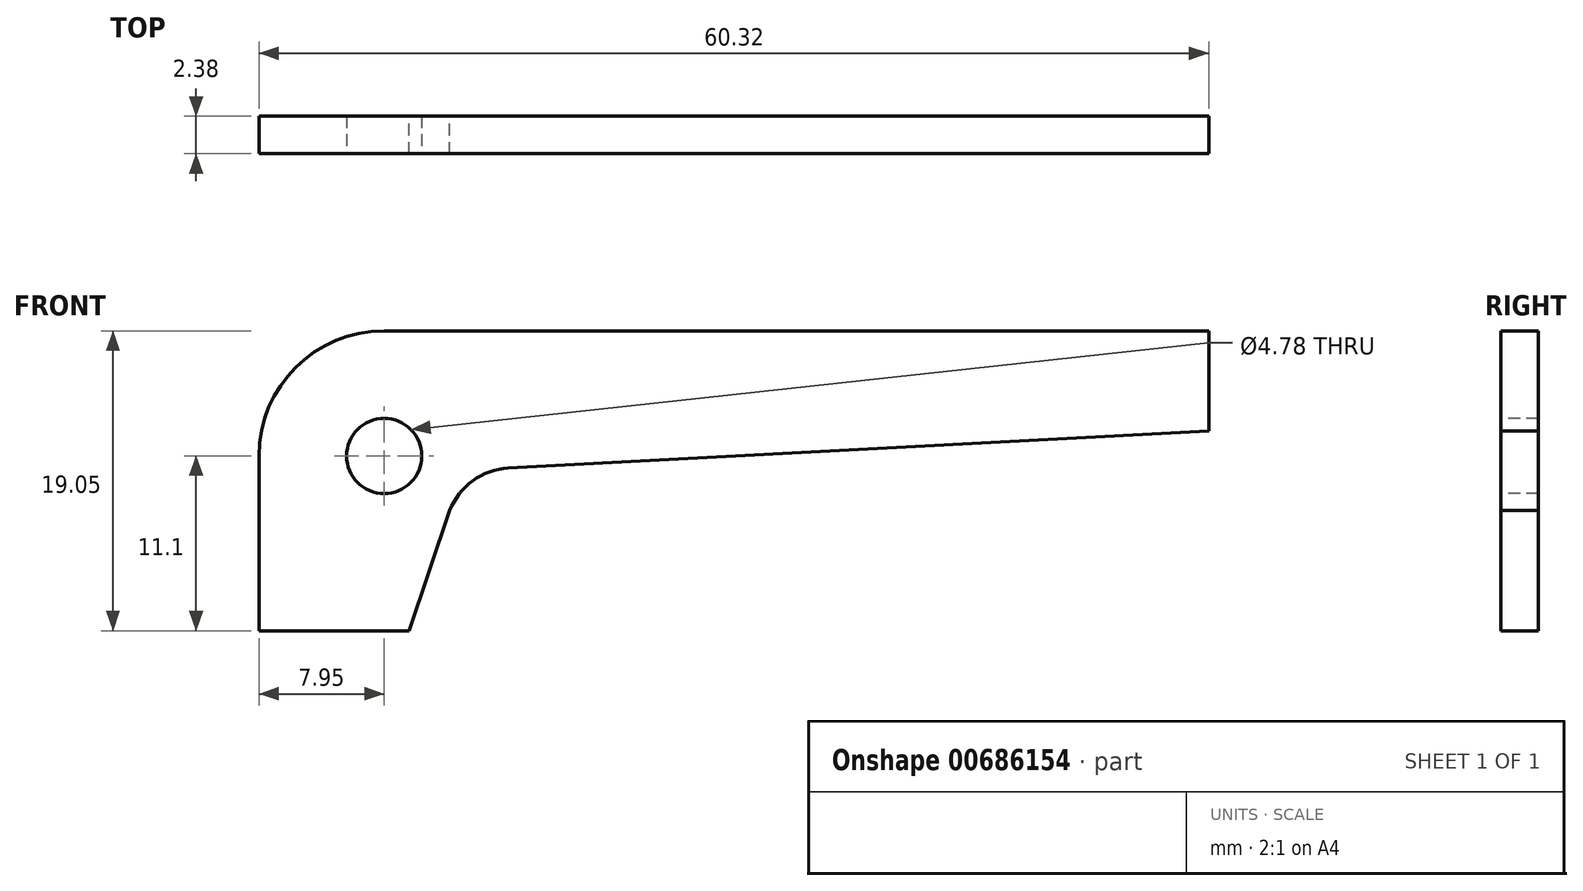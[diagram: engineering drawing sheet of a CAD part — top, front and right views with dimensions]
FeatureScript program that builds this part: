
annotation { "Feature Type Name" : "Feature", "Feature Type Description" : "" }
export const myFeature = defineFeature(function(context is Context, id is Id, definition is map)
    precondition{}
    {
        {
            var Q0;
            Q0=qCreatedBy(makeId("Front.planeOp"),FACE);
            var sketch = newSketch(context, id + "F0", { "sketchPlane" : qUnion([Q0])});
            skLineSegment(sketch, "E0.top", {"start": v(7.94, 19.05) * mm, "end": v(60.33, 19.05) * mm});
            skLineSegment(sketch, "E0.left", {"start": v(0, 0) * mm, "end": v(0, 11.11) * mm});
            skLineSegment(sketch, "E1", {"start": v(9.53, 0) * mm, "end": v(12.11, 7.63) * mm});
            skLineSegment(sketch, "E2", {"start": v(15.83, 10.32) * mm, "end": v(60.33, 12.7) * mm});
            skLineSegment(sketch, "E3", {"start": v(0, 0) * mm, "end": v(9.53, 0) * mm});
            skLineSegment(sketch, "E4", {"start": v(60.33, 19.05) * mm, "end": v(60.33, 12.7) * mm});
            skArc(sketch, "E5", {"start": v(15.83, 10.32) * mm, "mid": v(13.57, 9.52) * mm, "end": v(12.11, 7.63) * mm});
            skPoint(sketch, "E6.visualSharp", {"position": v(0, 19.05) * mm});
            skArc(sketch, "E6.filletArc", {"start": v(7.94, 19.05) * mm, "mid": v(2.32, 16.73) * mm, "end": v(0, 11.11) * mm});
            skSolve(sketch);
        }
        {
            var Q0;
            Q0=makeQuery(id+"F0.imprint","IMPRINT",FACE,{"disambiguationData":[TD([[makeQuery(id+"F0.imprint","IMPRINT",EDGE,{"derivedFrom":sQuery(id+"F0.wireOp",EDGE,"E0.top")}),-1.0]])]});
            extrude(context, id + "F1", {"entities" : qUnion([Q0]), "depth" : 2.38 * mm, "offsetDistance" : 25.4 * mm});
        }
        {
            var Q0;
            Q0=makeQuery(id+"F1.opExtrude","CAP_FACE",FACE,{"disambiguationData":[OSD([sQuery(id+"F0.wireOp",EDGE,"E0.top"),sQuery(id+"F0.wireOp",EDGE,"E0.left"),sQuery(id+"F0.wireOp",EDGE,"E1"),sQuery(id+"F0.wireOp",EDGE,"E2"),sQuery(id+"F0.wireOp",EDGE,"E3"),sQuery(id+"F0.wireOp",EDGE,"E4"),sQuery(id+"F0.wireOp",EDGE,"E5"),sQuery(id+"F0.wireOp",EDGE,"E6.filletArc")])],"isStart":false});
            var sketch = newSketch(context, id + "F2", { "sketchPlane" : qUnion([Q0])});
            skCircle(sketch, "E7", {"center": v(7.95, 11.1) * mm, "radius": 2.39 * mm});
            skSolve(sketch);
        }
        {
            var Q0;
            Q0=makeQuery(id+"F2.imprint","IMPRINT",FACE,{"disambiguationData":[TD([[makeQuery(id+"F2.imprint","IMPRINT",EDGE,{"derivedFrom":sQuery(id+"F2.wireOp",EDGE,"E7")}),1.0]])]});
            extrude(context, id + "F3", {"entities" : qUnion([Q0]), "operationType" : NewBodyOperationType.REMOVE, "oppositeDirection" : true, "depth" : 25.4 * mm, "offsetDistance" : 25.4 * mm});
        }
    });
